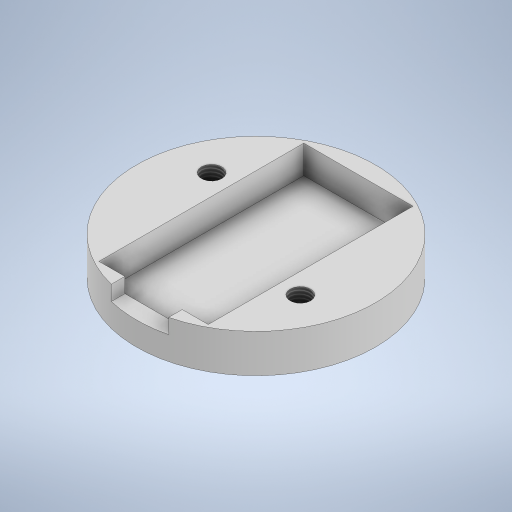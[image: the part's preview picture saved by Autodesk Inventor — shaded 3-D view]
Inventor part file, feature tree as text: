
AUTODESK INVENTOR PART (.ipt)
format: ipt  version: 2023 (Build 270158000, 158)  size: 403,968 bytes
history: native  units: mm
features: extrude x12, sketch x8, plane x2, fillet x2, thread x2
ambient origin geometry x8: Origin, YZ Plane, XZ Plane, XY Plane, X Axis, Y Axis, Z Axis, Center Point
bodies: Solid1 (feature_tree)
feature tree (26):
  sketch  "Sketch1"  dims[d0=30.0mm d1=15.0mm]
  extrude  "Extrusion1"  Depth=30.0mm
  extrude  "Extrusion2"  Depth=16.0mm
  extrude  "Extrusion4"  Depth=1.5mm TaperAngle=0.0deg
  extrude  "Extrusion5"  Depth=8.4mm
  extrude  "Extrusion6"  Depth=1.94mm TaperAngle=0.0deg
  extrude  "Extrusion7"  Depth=1.5mm TaperAngle=0.0deg
  plane  "Work Plane1"
  extrude  "Extrusion9"  Depth=0.3mm
  plane  "Work Plane2"
  fillet  "Fillet3"  Radius=1.2mm
  fillet  "Fillet4"  Radius=1.2mm
  sketch  "Sketch6"  dims[d18=1.5mm d19=0.0mm d20=1.25mm d21=0.0mm]
  extrude  "Extrusion10"  Depth=0.5mm
  extrude  "Extrusion11"  Depth=0.5mm
  extrude  "Extrusion12"  TaperAngle=0.0deg  [1 undecoded]
  thread  "Thread1"  [1 undecoded]
  thread  "Thread2"  [1 undecoded]
  sketch  "Sketch8"  dims[d26=1.2mm d27=0.0mm d29=12.0mm d32=15.0mm d37=0.0mm d38=0.0mm d39=1.0mm d40=1.0mm d44=5.75mm d45=11.5mm d46=0.0mm d47=0.0mm d48=10.0mm d49=0.0mm d50=0.0mm d51=1.5mm d52=1.5mm d53=5.625mm d54=9.75mm d56=30.25mm d57=0.0mm d58=27.125mm d59=0.0mm d60=3.0mm d61=3.0mm d62=3.0mm d63=3.0mm d64=4.5mm d65=4.5mm d66=2.5mm d67=0.0mm d68=9.0mm d69=0.0mm d70=9.0mm d71=0.0mm d72=11.25mm d73=11.0mm d74=11.0mm d75=30.0mm d76=2.0mm d77=1.0mm d78=15.0mm d79=1.0mm d80=0.0mm d81=10.0mm d82=5.0mm d83=5.0mm d84=2.5mm d85=0.5mm d86=0.0mm d28=0.5mm d30=0.5mm d31=0.872665mm d43=0.0mm]
  extrude  "Extrusion13"  Depth=1.0mm
  extrude  "Extrusion14"  Depth=0.5mm
  sketch  "Sketch2"  dims[d2=16.0mm d3=8.0mm]
  sketch  "Sketch3"  dims[d7=1.5mm d8=0.0mm d9=8.25mm d10=0.0mm]
  sketch  "Sketch4"  dims[d11=8.4mm d12=4.2mm]
  sketch  "Sketch5"  dims[d13=35.0mm d16=1.94mm d17=0.0mm]
  sketch  "Sketch7"  dims[d22=0.3mm d23=0.3mm d24=1.2mm d25=1.2mm]
note: 3 required parameter values undecoded (feature->parameter linkage not recoverable at this tier; creation-order binding heuristic only, values carry confidence <= 0.55)
